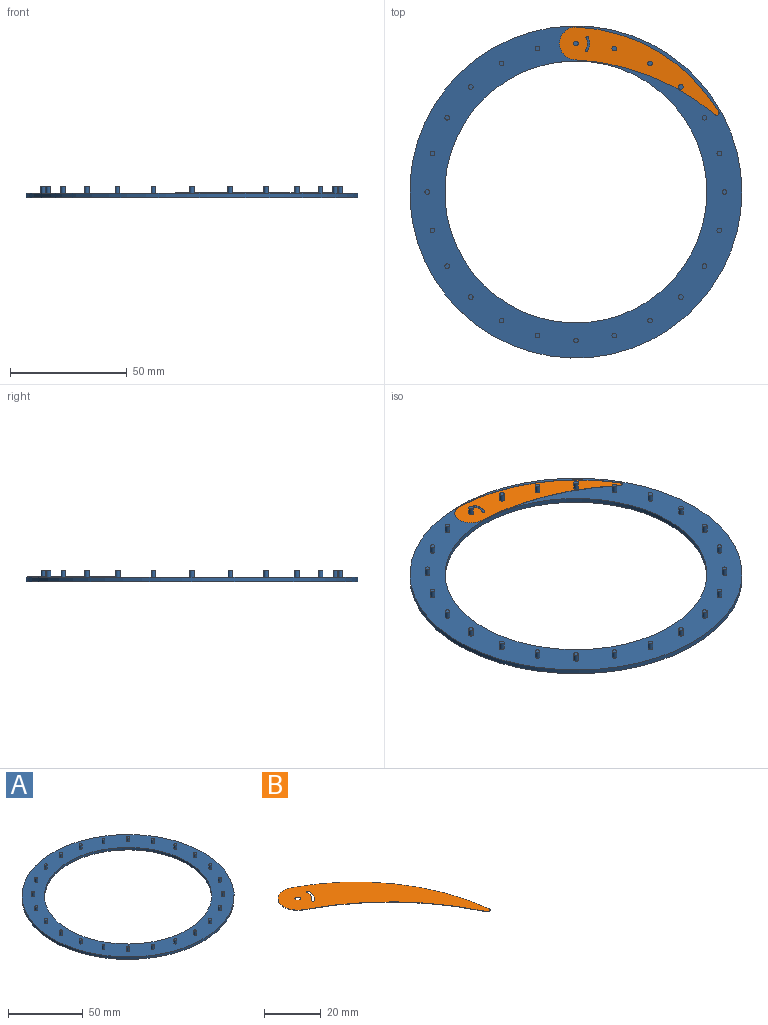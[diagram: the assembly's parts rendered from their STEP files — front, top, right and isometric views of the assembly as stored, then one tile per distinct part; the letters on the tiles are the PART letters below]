
ASSEMBLY  parts=2 mates=1
PART A: 52 faces, bbox 142x142x5 mm
  f0: cylinder r=1mm len=3mm, axis (0,0,-1), area 18.8mm2, adj f1,f48
  f1: plane 2x2mm, normal (0,0,1), area 3.1mm2, adj f0
  f2: cylinder r=1mm len=3mm, axis (0,0,-1), area 18.8mm2, adj f3,f48
  f3: plane 2x2mm, normal (0,0,1), area 3.1mm2, adj f2
  f4: cylinder r=1mm len=3mm, axis (0,0,-1), area 18.8mm2, adj f5,f48
  f5: plane 2x2mm, normal (0,0,1), area 3.1mm2, adj f4
  f6: cylinder r=1mm len=3mm, axis (0,0,-1), area 18.8mm2, adj f7,f48
  f7: plane 2x2mm, normal (0,0,1), area 3.1mm2, adj f6
  f8: cylinder r=1mm len=3mm, axis (0,0,-1), area 18.8mm2, adj f9,f48
  f9: plane 2x2mm, normal (0,0,1), area 3.1mm2, adj f8
  f10: cylinder r=1mm len=3mm, axis (0,0,-1), area 18.8mm2, adj f11,f48
  f11: plane 2x2mm, normal (0,0,1), area 3.1mm2, adj f10
  f12: cylinder r=1mm len=3mm, axis (0,0,-1), area 18.8mm2, adj f13,f48
  f13: plane 2x2mm, normal (0,0,1), area 3.1mm2, adj f12
  f14: cylinder r=1mm len=3mm, axis (0,0,-1), area 18.8mm2, adj f15,f48
  f15: plane 2x2mm, normal (0,0,1), area 3.1mm2, adj f14
  f16: cylinder r=1mm len=3mm, axis (0,0,-1), area 18.8mm2, adj f17,f48
  f17: plane 2x2mm, normal (0,0,1), area 3.1mm2, adj f16
  f18: cylinder r=1mm len=3mm, axis (0,0,-1), area 18.8mm2, adj f19,f48
  f19: plane 2x2mm, normal (0,0,1), area 3.1mm2, adj f18
  f20: cylinder r=1mm len=3mm, axis (0,0,-1), area 18.8mm2, adj f21,f48
  f21: plane 2x2mm, normal (0,0,1), area 3.1mm2, adj f20
  f22: cylinder r=1mm len=3mm, axis (0,0,-1), area 18.8mm2, adj f23,f48
  f23: plane 2x2mm, normal (0,0,1), area 3.1mm2, adj f22
  f24: cylinder r=1mm len=3mm, axis (0,0,-1), area 18.8mm2, adj f25,f48
  f25: plane 2x2mm, normal (0,0,1), area 3.1mm2, adj f24
  f26: cylinder r=1mm len=3mm, axis (0,0,-1), area 18.8mm2, adj f27,f48
  f27: plane 2x2mm, normal (0,0,1), area 3.1mm2, adj f26
  f28: cylinder r=1mm len=3mm, axis (0,0,-1), area 18.8mm2, adj f29,f48
  f29: plane 2x2mm, normal (0,0,1), area 3.1mm2, adj f28
  f30: cylinder r=1mm len=3mm, axis (0,0,-1), area 18.8mm2, adj f31,f48
  f31: plane 2x2mm, normal (0,0,1), area 3.1mm2, adj f30
  f32: cylinder r=1mm len=3mm, axis (0,0,-1), area 18.8mm2, adj f33,f48
  f33: plane 2x2mm, normal (0,0,1), area 3.1mm2, adj f32
  f34: cylinder r=1mm len=3mm, axis (0,0,-1), area 18.8mm2, adj f35,f48
  f35: plane 2x2mm, normal (0,0,1), area 3.1mm2, adj f34
  f36: cylinder r=1mm len=3mm, axis (0,0,-1), area 18.8mm2, adj f37,f48
  f37: plane 2x2mm, normal (0,0,1), area 3.1mm2, adj f36
  f38: cylinder r=1mm len=3mm, axis (0,0,-1), area 18.8mm2, adj f39,f48
  f39: plane 2x2mm, normal (0,0,1), area 3.1mm2, adj f38
  f40: cylinder r=1mm len=3mm, axis (0,0,-1), area 18.8mm2, adj f41,f48
  f41: plane 2x2mm, normal (0,0,1), area 3.1mm2, adj f40
  f42: cylinder r=1mm len=3mm, axis (0,0,-1), area 18.8mm2, adj f43,f48
  f43: plane 2x2mm, normal (0,0,1), area 3.1mm2, adj f42
  f44: cylinder r=1mm len=3mm, axis (0,0,-1), area 18.8mm2, adj f45,f48
  f45: plane 2x2mm, normal (0,0,1), area 3.1mm2, adj f44
  f46: cylinder r=71mm len=142mm, axis (0,0,-1), area 892.2mm2, adj f48,f49
  f47: cylinder r=56mm len=112mm, axis (0,0,-1), area 703.7mm2, adj f48,f49
  f48: plane 142x142mm, normal (0,0,1), area 5909.3mm2, adj f0,f2,f4,f6,f8,f10,f12,f14
  f49: plane 142x142mm, normal (0,0,-1), area 5984.7mm2, adj f46,f47
  f50: cylinder r=1mm len=3mm, axis (0,0,-1), area 18.8mm2, adj f48,f51
  f51: plane 2x2mm, normal (0,0,1), area 3.1mm2, adj f50
PART B: 11 faces, bbox 50.4x60.1x0.1 mm
  f0: cylinder r=75mm len=58.22mm, axis (0,0,-1), area 7.4mm2, adj f1,f8,f9,f10
  f1: cylinder r=7mm len=13.22mm, axis (0,0,-1), area 2.2mm2, adj f0,f2,f9,f10
  f2: cylinder r=100mm len=46.32mm, axis (0,0,-1), area 6.6mm2, adj f1,f8,f9,f10
  f3: cylinder r=0.5mm len=1mm, axis (0,0,-1), area 0.2mm2, adj f4,f7,f9,f10
  f4: cylinder r=5.94mm len=5.28mm, axis (0,0,-1), area 0.6mm2, adj f3,f5,f9,f10
  f5: cylinder r=0.5mm len=0.92mm, axis (0,0,-1), area 0.2mm2, adj f4,f7,f9,f10
  f6: cylinder r=1mm len=2mm, axis (0,0,-1), area 0.6mm2, adj f9,f10
  f7: cylinder r=4.94mm len=4.39mm, axis (0,0,-1), area 0.5mm2, adj f3,f5,f9,f10
  f8: cylinder r=1mm len=1.9mm, axis (0,0,-1), area 0.3mm2, adj f0,f2,f9,f10
  f9: plane 60.11x50.4mm, normal (0,0,1), area 755.1mm2, adj f0,f1,f2,f3,f4,f5,f6,f7
  f10: plane 60.11x50.4mm, normal (0,0,-1), area 755.1mm2, adj f0,f1,f2,f3,f4,f5,f6,f7
PLACE A at identity fixed
PLACE B rot(axis=(0,0,1),24.6deg) t=(-27.42,-556.6,2)mm
MATE revolute B.f1 <-> A.f22  axis (0,0,-1) through (0,63.5,2)mm
